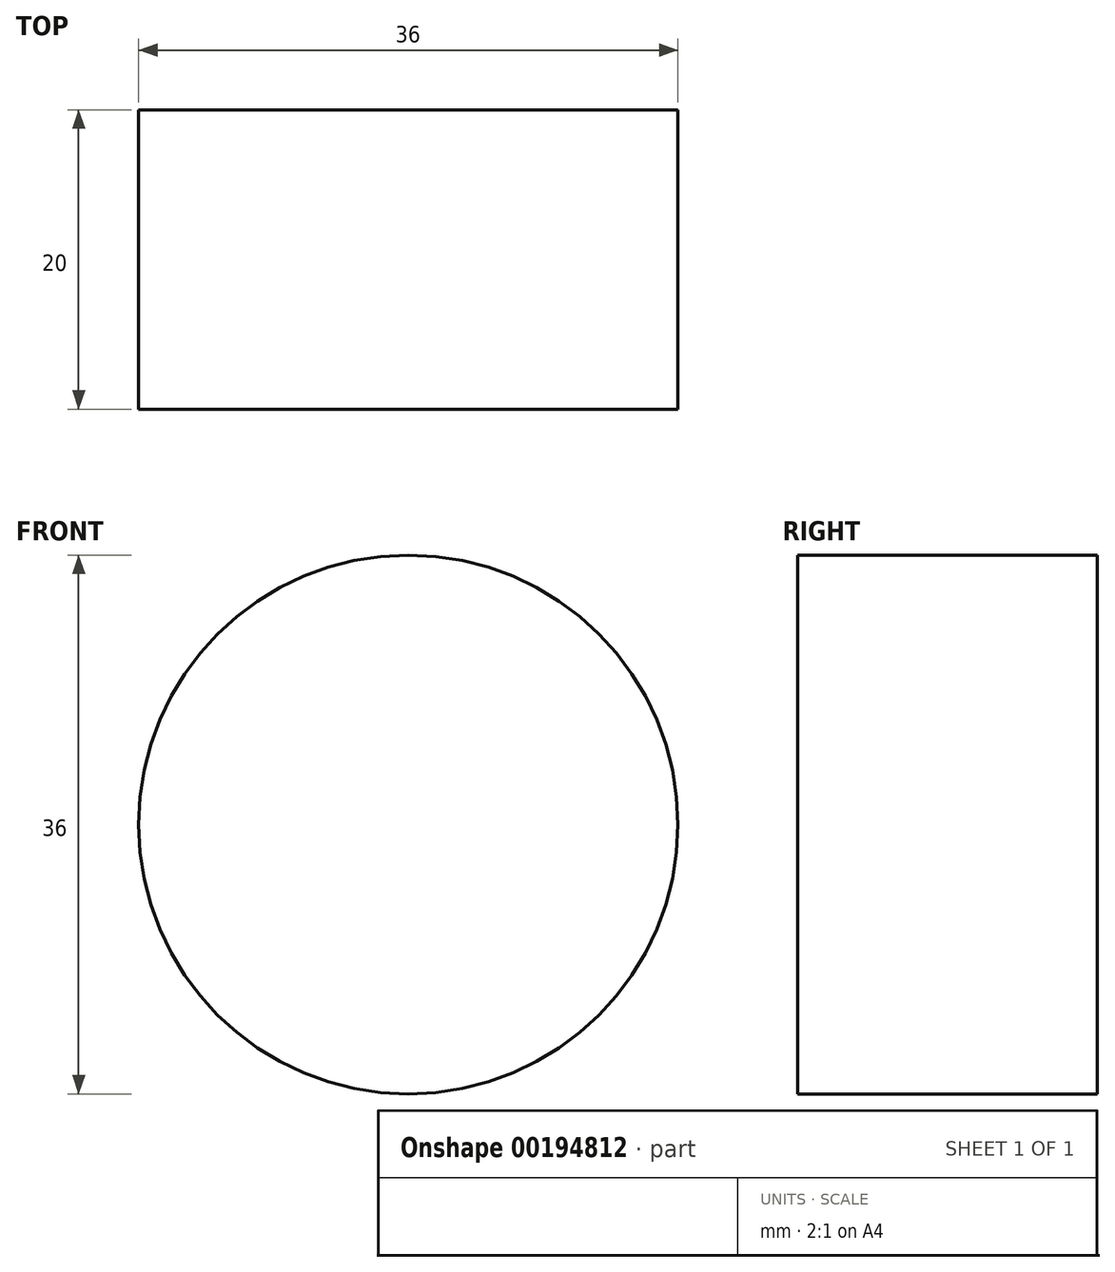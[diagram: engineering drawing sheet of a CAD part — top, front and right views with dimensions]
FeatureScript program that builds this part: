
annotation { "Feature Type Name" : "Feature", "Feature Type Description" : "" }
export const myFeature = defineFeature(function(context is Context, id is Id, definition is map)
    precondition{}
    {
        {
            var Q0;
            Q0=qCreatedBy(makeId("Front.planeOp"),FACE);
            var sketch = newSketch(context, id + "F0", { "sketchPlane" : qUnion([Q0])});
            skCircle(sketch, "E0", {"center": v(0, 0) * mm, "radius": 18 * mm});
            skSolve(sketch);
        }
        {
            var Q0;
            Q0 = qSketchRegion(id + "F0", true);
            extrude(context, id + "F1", {"entities" : qUnion([Q0]), "oppositeDirection" : true, "depth" : 20 * mm});
        }
    });
